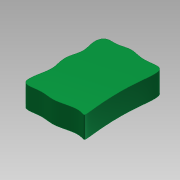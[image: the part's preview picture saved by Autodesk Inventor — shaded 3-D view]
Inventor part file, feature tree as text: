
AUTODESK INVENTOR PART (.ipt)
format: ipt  version: 2011 (Build 150239000, 239)  size: 87,040 bytes
history: native  units: mm
features: other x1, extrude x1, sketch x1
ambient origin geometry x8: Origin, YZ Plane, XZ Plane, XY Plane, X Axis, Y Axis, Z Axis, Center Point
feature tree (3):
  other  "РабПлоскость3"
  extrude  "Выдавливание4"  Depth=1.5mm TaperAngle=0.0deg
  sketch  "Эскиз4"
